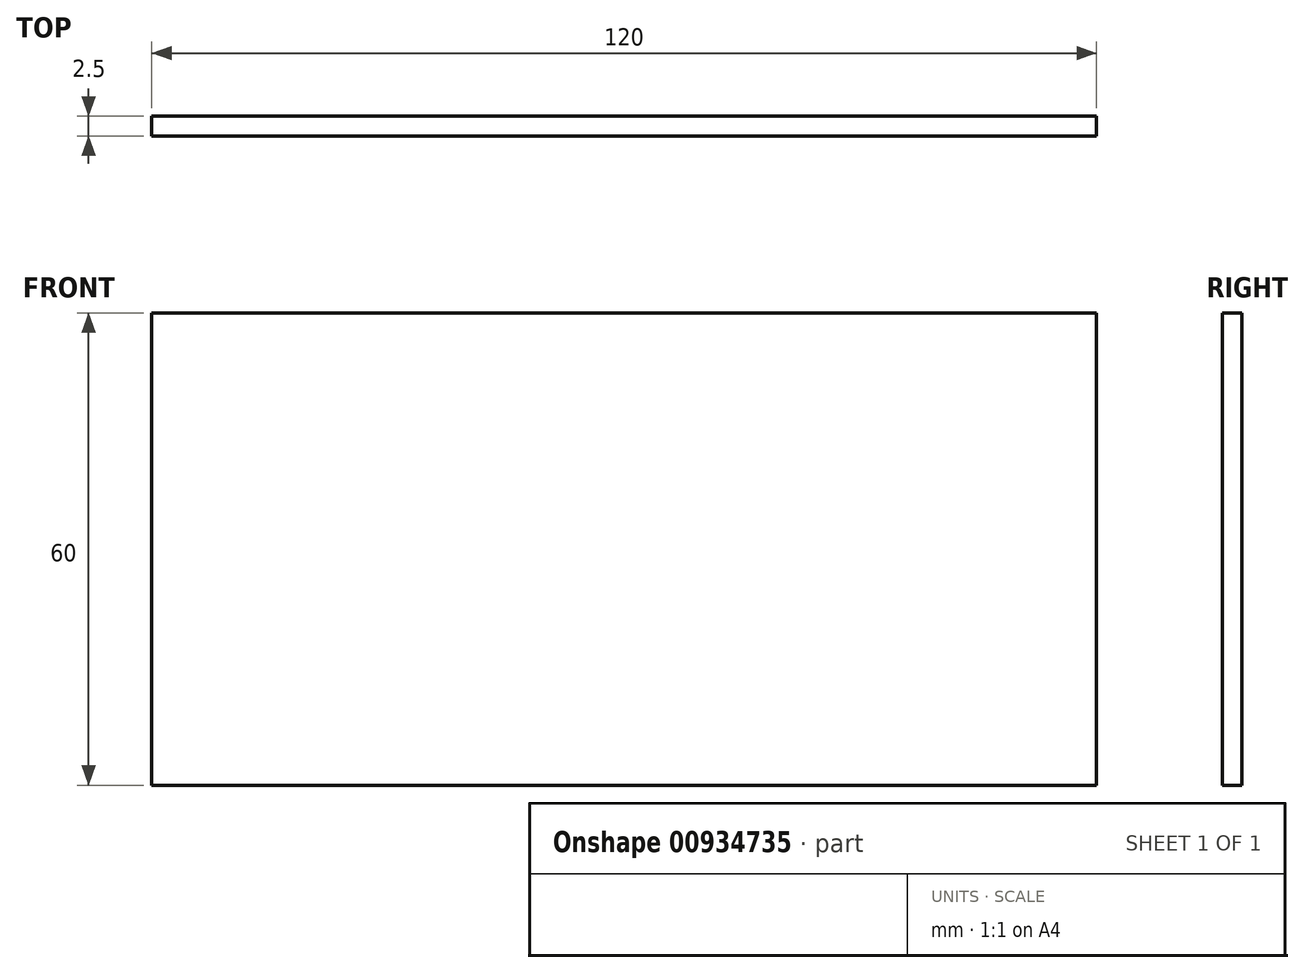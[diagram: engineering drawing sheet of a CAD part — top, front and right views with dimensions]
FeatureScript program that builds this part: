
annotation { "Feature Type Name" : "Feature", "Feature Type Description" : "" }
export const myFeature = defineFeature(function(context is Context, id is Id, definition is map)
    precondition{}
    {
        {
            var Q0;
            Q0=qCreatedBy(makeId("Front.planeOp"),FACE);
            var sketch = newSketch(context, id + "F0", { "sketchPlane" : qUnion([Q0])});
            skLineSegment(sketch, "E0.bottom", {"start": v(-60, 30) * mm, "end": v(60, 30) * mm});
            skLineSegment(sketch, "E0.top", {"start": v(-60, -30) * mm, "end": v(60, -30) * mm});
            skLineSegment(sketch, "E0.left", {"start": v(-60, 30) * mm, "end": v(-60, -30) * mm});
            skLineSegment(sketch, "E0.right", {"start": v(60, 30) * mm, "end": v(60, -30) * mm});
            skPoint(sketch, "E0.middle", {"position": v(0, 0) * mm});
            skSolve(sketch);
        }
        {
            var Q0;
            Q0=makeQuery(id+"F0.imprint","IMPRINT",FACE,{"disambiguationData":[TD([[makeQuery(id+"F0.imprint","IMPRINT",EDGE,{"derivedFrom":sQuery(id+"F0.wireOp",EDGE,"E0.bottom")}),-1.0]])]});
            extrude(context, id + "F1", {"entities" : qUnion([Q0]), "depth" : 2.5 * mm, "offsetDistance" : 25 * mm});
        }
    });
